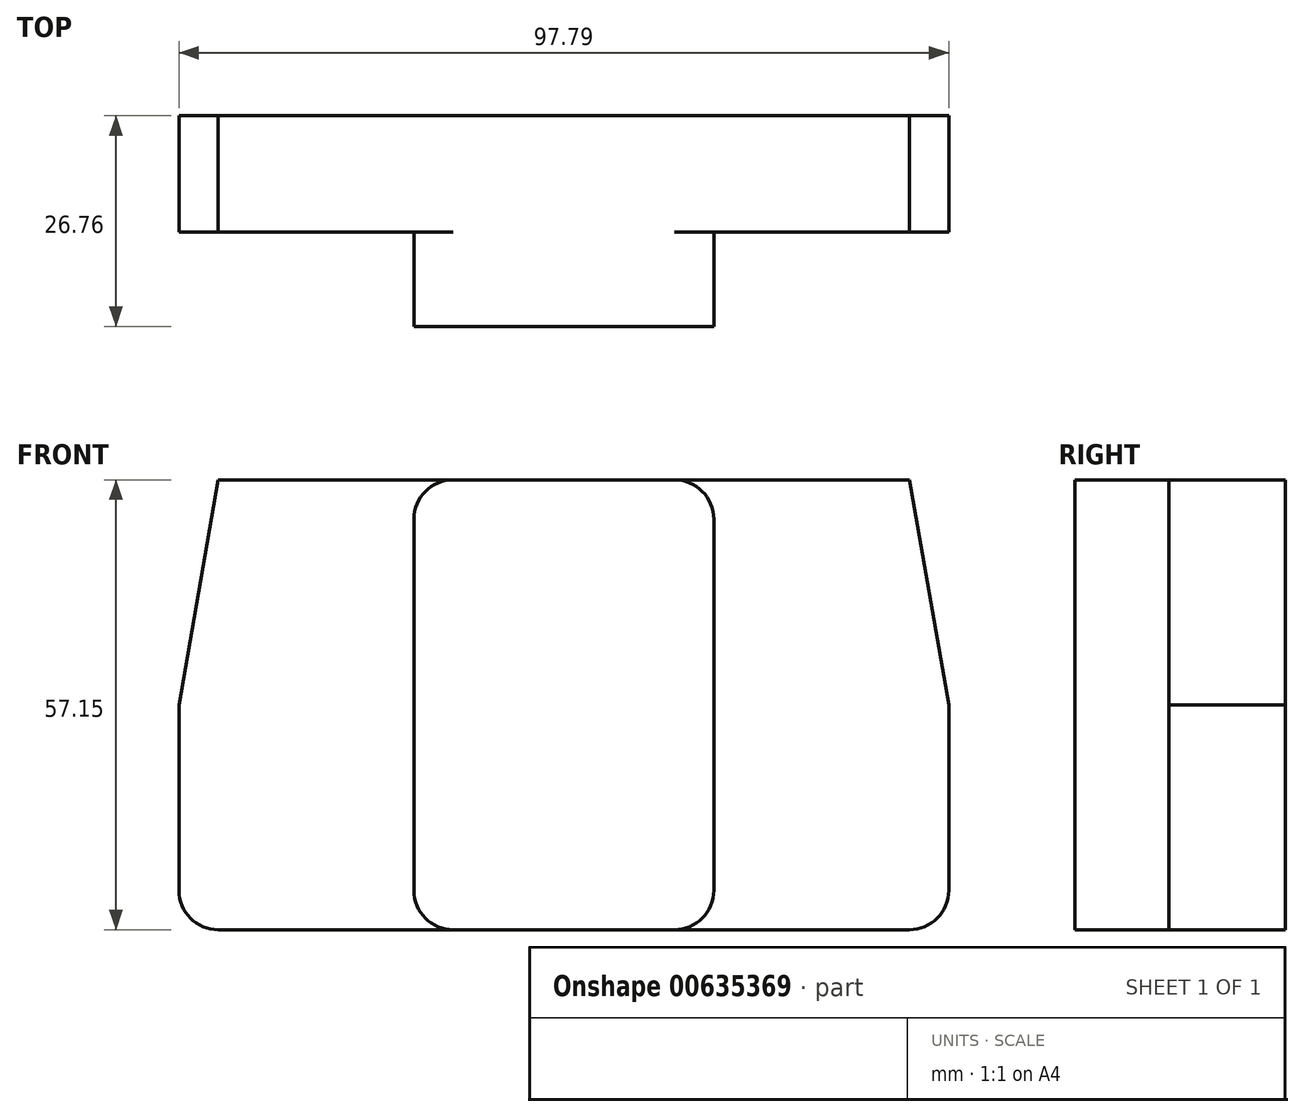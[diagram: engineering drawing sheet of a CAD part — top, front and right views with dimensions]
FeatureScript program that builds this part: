
annotation { "Feature Type Name" : "Feature", "Feature Type Description" : "" }
export const myFeature = defineFeature(function(context is Context, id is Id, definition is map)
    precondition{}
    {
        {
            var Q0;
            Q0=qCreatedBy(makeId("Front.planeOp"),FACE);
            var sketch = newSketch(context, id + "F0", { "sketchPlane" : qUnion([Q0])});
            skLineSegment(sketch, "E0.bottom", {"start": v(0, 0) * mm, "end": v(97.8, 0) * mm});
            skLineSegment(sketch, "E0.top", {"start": v(0, 57.15) * mm, "end": v(97.8, 57.15) * mm});
            skLineSegment(sketch, "E0.left", {"start": v(0, 0) * mm, "end": v(0, 57.15) * mm});
            skLineSegment(sketch, "E0.right", {"start": v(97.8, 0) * mm, "end": v(97.8, 57.15) * mm});
            skSolve(sketch);
        }
        {
            var Q0;
            Q0 = qSketchRegion(id + "F0", true);
            extrude(context, id + "F1", {"entities" : qUnion([Q0]), "depth" : 14.78 * mm, "offsetDistance" : 25 * mm});
        }
        {
            var Q0;
            Q0=makeQuery(id+"F1.opExtrude","CAP_FACE",FACE,{"disambiguationData":[OSD([sQuery(id+"F0.wireOp",EDGE,"E0.bottom"),sQuery(id+"F0.wireOp",EDGE,"E0.top"),sQuery(id+"F0.wireOp",EDGE,"E0.left"),sQuery(id+"F0.wireOp",EDGE,"E0.right")])],"isStart":false});
            var sketch = newSketch(context, id + "F2", { "sketchPlane" : qUnion([Q0])});
            skLineSegment(sketch, "E1.bottom", {"start": v(29.85, 0) * mm, "end": v(67.95, 0) * mm});
            skLineSegment(sketch, "E1.top", {"start": v(29.85, 57.15) * mm, "end": v(67.95, 57.15) * mm});
            skLineSegment(sketch, "E1.left", {"start": v(29.85, 0) * mm, "end": v(29.85, 57.15) * mm});
            skLineSegment(sketch, "E1.right", {"start": v(67.95, 0) * mm, "end": v(67.95, 57.15) * mm});
            skLineSegment(sketch, "E2", {"start": v(29.85, 57.15) * mm, "end": v(0, 57.15) * mm});
            skLineSegment(sketch, "E3", {"start": v(67.95, 57.15) * mm, "end": v(97.8, 57.15) * mm});
            skSolve(sketch);
        }
        {
            var Q0;
            Q0 = qSketchRegion(id + "F2", true);
            extrude(context, id + "F3", {"entities" : qUnion([Q0]), "operationType" : NewBodyOperationType.ADD, "depth" : 11.97 * mm, "offsetDistance" : 25 * mm});
        }
        {
            var Q0;
            Q0=makeQuery(id+"F1.opExtrude","SWEPT_EDGE",EDGE,{"disambiguationData":[OSD([sQuery(id+"F0.wireOp",EDGE,"E0.bottom"),sQuery(id+"F0.wireOp",EDGE,"E0.left")])]});
            var Q1;
            Q1=makeQuery(id+"F3.opExtrude","SWEPT_EDGE",EDGE,{"disambiguationData":[OSD([sQuery(id+"F0.wireOp",EDGE,"E0.bottom"),sQuery(id+"F2.wireOp",EDGE,"E1.bottom"),sQuery(id+"F2.wireOp",EDGE,"E1.left")])]});
            var Q2;
            Q2=makeQuery(id+"F3.opExtrude","SWEPT_EDGE",EDGE,{"disambiguationData":[OSD([sQuery(id+"F0.wireOp",EDGE,"E0.bottom"),sQuery(id+"F2.wireOp",EDGE,"E1.bottom"),sQuery(id+"F2.wireOp",EDGE,"E1.right")])]});
            var Q3;
            Q3=makeQuery(id+"F1.opExtrude","SWEPT_EDGE",EDGE,{"disambiguationData":[OSD([sQuery(id+"F0.wireOp",EDGE,"E0.bottom"),sQuery(id+"F0.wireOp",EDGE,"E0.right")])]});
            var Q4;
            Q4=makeQuery(id+"F1.opExtrude","SWEPT_EDGE",EDGE,{"disambiguationData":[OSD([sQuery(id+"F0.wireOp",EDGE,"E0.top"),sQuery(id+"F0.wireOp",EDGE,"E0.right")])]});
            var Q5;
            Q5=makeQuery(id+"F3.opExtrude","SWEPT_EDGE",EDGE,{"disambiguationData":[OSD([sQuery(id+"F2.wireOp",EDGE,"E1.top"),sQuery(id+"F2.wireOp",EDGE,"E1.right"),sQuery(id+"F2.wireOp",EDGE,"E3")])]});
            var Q6;
            Q6=makeQuery(id+"F3.opExtrude","SWEPT_EDGE",EDGE,{"disambiguationData":[OSD([sQuery(id+"F2.wireOp",EDGE,"E1.top"),sQuery(id+"F2.wireOp",EDGE,"E1.left"),sQuery(id+"F2.wireOp",EDGE,"E2")])]});
            var Q7;
            Q7=makeQuery(id+"F1.opExtrude","SWEPT_EDGE",EDGE,{"disambiguationData":[OSD([sQuery(id+"F0.wireOp",EDGE,"E0.top"),sQuery(id+"F0.wireOp",EDGE,"E0.left")])]});
            fillet(context, id + "F4", {"entities" : qUnion([Q0, Q1, Q2, Q3, Q4, Q5, Q6, Q7]), "radius" : 5 * mm, "tangentPropagation" : true, "allowEdgeOverflow" : false});
        }
        {
            var Q0;
            Q0=makeQuery(id+"F1.opExtrude","CAP_FACE",FACE,{"disambiguationData":[OSD([sQuery(id+"F0.wireOp",EDGE,"E0.bottom"),sQuery(id+"F0.wireOp",EDGE,"E0.top"),sQuery(id+"F0.wireOp",EDGE,"E0.left"),sQuery(id+"F0.wireOp",EDGE,"E0.right")])],"isStart":true});
            var sketch = newSketch(context, id + "F5", { "sketchPlane" : qUnion([Q0])});
            skLineSegment(sketch, "E4", {"start": v(-97.8, 28.58) * mm, "end": v(-92.8, 57.15) * mm});
            skLineSegment(sketch, "E5", {"start": v(-92.8, 57.15) * mm, "end": v(-97.8, 58.02) * mm});
            skLineSegment(sketch, "E6", {"start": v(-97.8, 58.02) * mm, "end": v(-97.8, 28.58) * mm});
            skLineSegment(sketch, "E7", {"start": v(0, 28.58) * mm, "end": v(-5, 57.15) * mm});
            skLineSegment(sketch, "E8", {"start": v(-5, 57.15) * mm, "end": v(0, 58.02) * mm});
            skLineSegment(sketch, "E9", {"start": v(0, 58.02) * mm, "end": v(0, 28.58) * mm});
            skSolve(sketch);
        }
        {
            var Q0;
            Q0 = qSketchRegion(id + "F5", true);
            extrude(context, id + "F6", {"entities" : qUnion([Q0]), "operationType" : NewBodyOperationType.REMOVE, "endBound" : BoundingType.THROUGH_ALL, "oppositeDirection" : true, "depth" : 25 * mm, "offsetDistance" : 25 * mm});
        }
    });
